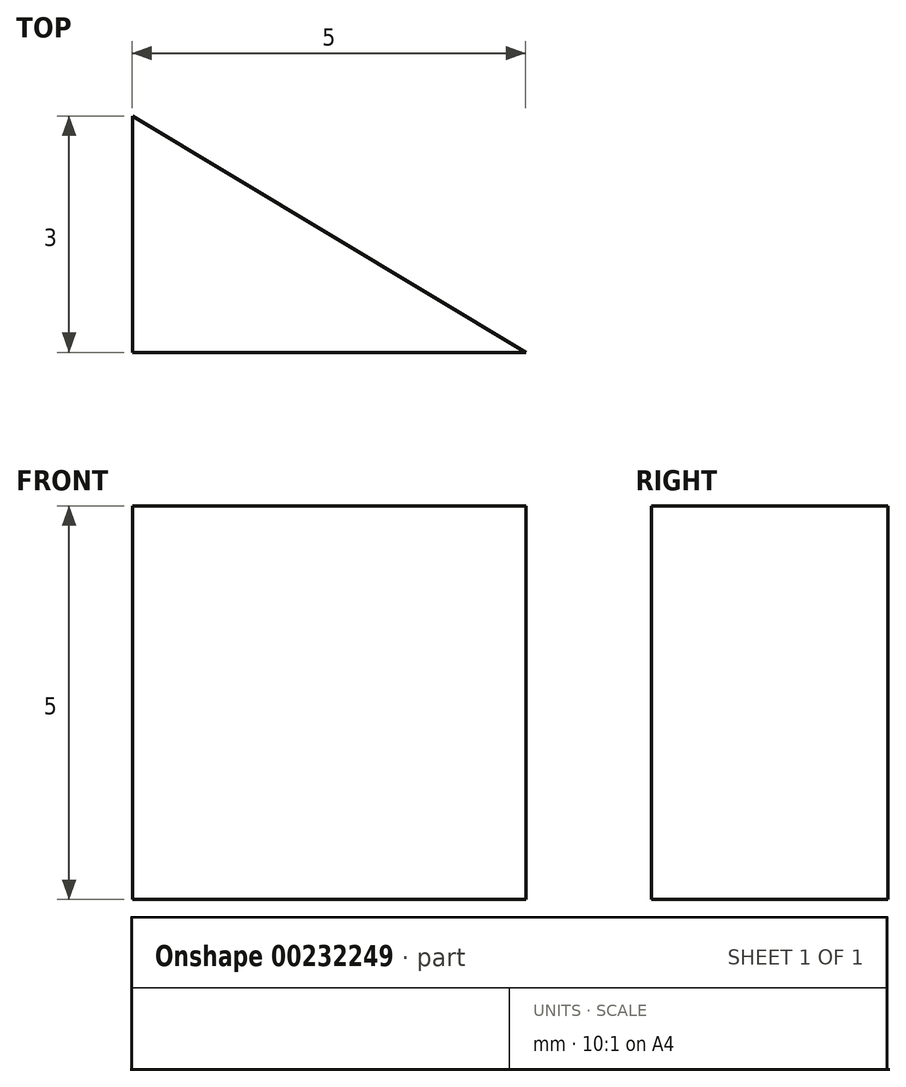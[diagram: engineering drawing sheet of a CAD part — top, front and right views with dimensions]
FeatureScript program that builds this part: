
annotation { "Feature Type Name" : "Feature", "Feature Type Description" : "" }
export const myFeature = defineFeature(function(context is Context, id is Id, definition is map)
    precondition{}
    {
        {
            var Q0;
            Q0=qCreatedBy(makeId("Top.planeOp"),FACE);
            var sketch = newSketch(context, id + "F0", { "sketchPlane" : qUnion([Q0])});
            skLineSegment(sketch, "E0.top", {"start": v(-15.23, 7.85) * mm, "end": v(-10.23, 7.85) * mm});
            skLineSegment(sketch, "E0.left", {"start": v(-15.23, 10.85) * mm, "end": v(-15.23, 7.85) * mm});
            skLineSegment(sketch, "E1", {"start": v(-15.23, 10.85) * mm, "end": v(-10.23, 7.85) * mm});
            skSolve(sketch);
        }
        {
            var Q0;
            Q0=makeQuery(id+"F0.imprint","IMPRINT",FACE,{"disambiguationData":[TD([[makeQuery(id+"F0.imprint","IMPRINT",EDGE,{"derivedFrom":sQuery(id+"F0.wireOp",EDGE,"E0.top")}),1.0]])]});
            extrude(context, id + "F1", {"entities" : qUnion([Q0]), "depth" : 5 * mm});
        }
    });
